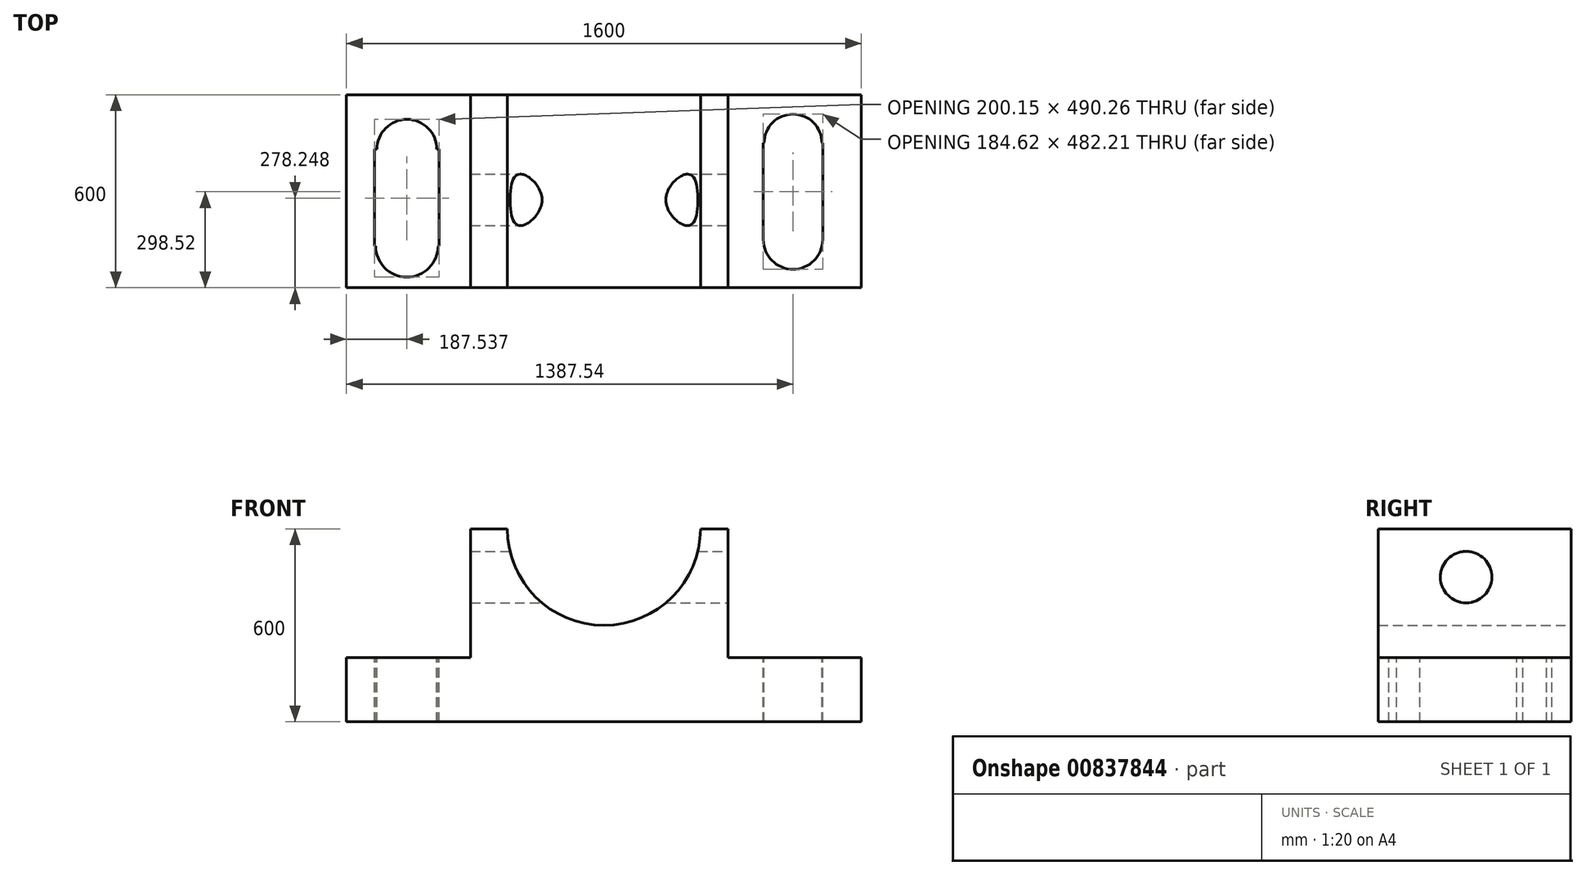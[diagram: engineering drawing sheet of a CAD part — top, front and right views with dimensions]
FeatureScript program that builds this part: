
annotation { "Feature Type Name" : "Feature", "Feature Type Description" : "" }
export const myFeature = defineFeature(function(context is Context, id is Id, definition is map)
    precondition{}
    {
        {
            var Q0;
            Q0=qCreatedBy(makeId("Front.planeOp"),FACE);
            var sketch = newSketch(context, id + "F0", { "sketchPlane" : qUnion([Q0])});
            skLineSegment(sketch, "E0.top", {"start": v(800, -300) * mm, "end": v(-800, -300) * mm});
            skLineSegment(sketch, "E0.left", {"start": v(800, -100) * mm, "end": v(800, -300) * mm});
            skLineSegment(sketch, "E0.right", {"start": v(-800, -100) * mm, "end": v(-800, -300) * mm});
            skPoint(sketch, "E0.middle", {"position": v(0, 0) * mm});
            skArc(sketch, "E1", {"start": v(-300, 300) * mm, "mid": v(0, 0) * mm, "end": v(300, 300) * mm});
            skLineSegment(sketch, "E2.trimOffspring", {"start": v(-300, 300) * mm, "end": v(-414.36, 300) * mm});
            skLineSegment(sketch, "E3", {"start": v(-414.36, 300) * mm, "end": v(-414.36, -100) * mm});
            skLineSegment(sketch, "E4", {"start": v(-414.36, -100) * mm, "end": v(-800, -100) * mm});
            skLineSegment(sketch, "E5", {"start": v(-800, -100) * mm, "end": v(-414.36, -100) * mm});
            skLineSegment(sketch, "E6", {"start": v(385.64, -100) * mm, "end": v(385.64, 300) * mm});
            skLineSegment(sketch, "E7", {"start": v(800, -100) * mm, "end": v(385.64, -100) * mm});
            skPoint(sketch, "E8.orphan", {"position": v(-800, 300) * mm});
            skPoint(sketch, "E9.orphan", {"position": v(800, 300) * mm});
            skLineSegment(sketch, "E10", {"start": v(385.64, 300) * mm, "end": v(300, 300) * mm});
            skSolve(sketch);
        }
        {
            var Q0;
            Q0=makeQuery(id+"F0.imprint","IMPRINT",FACE,{"disambiguationData":[TD([[makeQuery(id+"F0.imprint","IMPRINT",EDGE,{"derivedFrom":sQuery(id+"F0.wireOp",EDGE,"E0.top")}),-1.0]])]});
            extrude(context, id + "F1", {"entities" : qUnion([Q0]), "depth" : 600 * mm, "offsetDistance" : 25 * mm});
        }
        {
            var Q0;
            Q0=makeQuery(id+"F1.opExtrude","SWEPT_FACE",FACE,{"disambiguationData":[OSD([sQuery(id+"F0.wireOp",EDGE,"E6")])]});
            var sketch = newSketch(context, id + "F2", { "sketchPlane" : qUnion([Q0])});
            skCircle(sketch, "E11", {"center": v(-326.72, 150) * mm, "radius": 80 * mm});
            skSolve(sketch);
        }
        {
            var Q0;
            Q0 = qSketchRegion(id + "F2", true);
            extrude(context, id + "F3", {"entities" : qUnion([Q0]), "operationType" : NewBodyOperationType.REMOVE, "endBound" : BoundingType.THROUGH_ALL, "oppositeDirection" : true, "depth" : 25 * mm, "offsetDistance" : 25 * mm});
        }
        {
            var Q0;
            Q0=makeQuery(id+"F1.opExtrude","SWEPT_FACE",FACE,{"disambiguationData":[OSD([sQuery(id+"F0.wireOp",EDGE,"E7")])]});
            var sketch = newSketch(context, id + "F4", { "sketchPlane" : qUnion([Q0])});
            skPoint(sketch, "E12.middle", {"position": v(592.82, -300) * mm});
            skPoint(sketch, "E12.middle.positionSnap0", {"position": v(592.82, 0) * mm});
            skPoint(sketch, "E12.middle.positionSnap1", {"position": v(800, -300) * mm});
            skPoint(sketch, "E12.centerSnap0", {"position": v(592.82, 0) * mm});
            skPoint(sketch, "E12.centerSnap1", {"position": v(800, -300) * mm});
            skSolve(sketch);
        }
        {
            var Q0;
            {var subQ0=sQuery(id+"F0.wireOp",EDGE,"E7");Q0=makeQuery(id+"F4.imprint","IMPRINT",FACE,{"disambiguationData":[TD([[makeQuery(id+"F4.imprint","IMPRINT",EDGE,{"derivedFrom":makeQuery(id+"F1.opExtrude","CAP_EDGE",EDGE,{"disambiguationData":[OSD([subQ0])],"isStart":true})}),1.0]])]});}
            var sketch = newSketch(context, id + "F5", { "sketchPlane" : qUnion([Q0])});
            skLineSegment(sketch, "E13.bottom", {"start": v(679.84, -150.28) * mm, "end": v(677.44, -150.28) * mm});
            skLineSegment(sketch, "E13.left", {"start": v(679.84, -150.28) * mm, "end": v(679.84, -450.28) * mm});
            skLineSegment(sketch, "E13.right", {"start": v(495.23, -150.28) * mm, "end": v(495.23, -450.28) * mm});
            skPoint(sketch, "E13.middle", {"position": v(587.54, -300.28) * mm});
            skArc(sketch, "E14", {"start": v(677.44, -150.28) * mm, "mid": v(587.54, -60.37) * mm, "end": v(497.63, -150.28) * mm});
            skArc(sketch, "E15", {"start": v(495.23, -450.28) * mm, "mid": v(587.54, -542.59) * mm, "end": v(679.84, -450.28) * mm});
            skLineSegment(sketch, "E16.bottom", {"start": v(-512.39, -169.73) * mm, "end": v(-519.35, -169.73) * mm});
            skLineSegment(sketch, "E16.top", {"start": v(-512.39, -469.73) * mm, "end": v(-515.32, -469.73) * mm});
            skLineSegment(sketch, "E16.left", {"start": v(-512.39, -169.73) * mm, "end": v(-512.39, -469.73) * mm});
            skLineSegment(sketch, "E16.right", {"start": v(-712.54, -169.73) * mm, "end": v(-712.54, -469.73) * mm});
            skPoint(sketch, "E16.middle", {"position": v(-612.46, -319.73) * mm});
            skArc(sketch, "E17", {"start": v(-519.35, -169.73) * mm, "mid": v(-612.46, -76.62) * mm, "end": v(-705.57, -169.73) * mm});
            skArc(sketch, "E18", {"start": v(-709.6, -469.73) * mm, "mid": v(-612.46, -566.88) * mm, "end": v(-515.32, -469.73) * mm});
            skLineSegment(sketch, "E19.trimOffspring", {"start": v(497.63, -150.28) * mm, "end": v(495.23, -150.28) * mm});
            skLineSegment(sketch, "E20.trimOffspring", {"start": v(-705.57, -169.73) * mm, "end": v(-712.54, -169.73) * mm});
            skLineSegment(sketch, "E21.trimOffspring", {"start": v(-709.6, -469.73) * mm, "end": v(-712.54, -469.73) * mm});
            skSolve(sketch);
        }
        {
            var Q0;
            Q0 = qSketchRegion(id + "F5", true);
            extrude(context, id + "F6", {"entities" : qUnion([Q0]), "operationType" : NewBodyOperationType.REMOVE, "endBound" : BoundingType.THROUGH_ALL, "oppositeDirection" : true, "depth" : 25 * mm, "offsetDistance" : 25 * mm});
        }
    });
